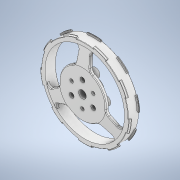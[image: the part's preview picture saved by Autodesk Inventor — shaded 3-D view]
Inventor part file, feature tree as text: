
AUTODESK INVENTOR PART (.ipt)
format: ipt  version: 2021 (Build 250183000, 183)  size: 946,176 bytes
history: native  units: mm
features: sketch x19, extrude x14, fillet x7, pattern_circular x5, revolve x3, other x2, chamfer x2, projected_geometry x2
ambient origin geometry x8: Origin, YZ Plane, XZ Plane, XY Plane, X Axis, Y Axis, Z Axis, Center Point
bodies: Body1 (feature_tree)
feature tree (54):
  other  "ソリッド1"
  extrude  "押し出し1"  Depth=50.6mm
  extrude  "押し出し2"  Depth=7.3mm TaperAngle=0.0deg
  sketch  "スケッチ3"
  revolve  "回転1"
  extrude  "押し出し3"  Depth=3.0mm
  revolve  "回転2"
  chamfer  "面取り1"  Distance=1.3mm
  chamfer  "面取り2"  Distance=26.0mm
  extrude  "押し出し4"  TaperAngle=90.0deg  [1 undecoded]
  pattern_circular  "円形状パターン1"  [2 undecoded]
  extrude  "押し出し5"  Depth=3.0mm
  pattern_circular  "円形状パターン2"  [2 undecoded]
  extrude  "押し出し6"  Depth=4.0mm
  extrude  "押し出し7"  Depth=30.0mm TaperAngle=360.0deg
  revolve  "回転3"
  extrude  "押し出し8"  TaperAngle=0.0deg  [1 undecoded]
  pattern_circular  "円形状パターン3"  [2 undecoded]
  extrude  "押し出し9"  Depth=1.0mm
  extrude  "押し出し10"  Depth=1.0mm
  extrude  "押し出し11"  TaperAngle=90.0deg  [1 undecoded]
  pattern_circular  "円形状パターン4"  Angle=45.0deg  [1 undecoded]
  extrude  "押し出し12"  Depth=0.7mm TaperAngle=45.0deg
  extrude  "押し出し13"  Depth=5.0mm
  pattern_circular  "円形状パターン5"  [2 undecoded]
  sketch  "スケッチ18"
  other  "作業平面1"
  extrude  "押し出し14"  TaperAngle=180.0deg  [1 undecoded]
  fillet  "フィレット1"  Radius=1.3mm
  fillet  "フィレット2"  Radius=90.0mm
  fillet  "フィレット3"  Radius=5.0mm
  fillet  "フィレット4"  Radius=5.0mm
  fillet  "フィレット5"  Radius=1.3mm
  fillet  "フィレット6"  Radius=90.0mm
  fillet  "フィレット7"  Radius=4.5mm
  sketch  "スケッチ1"
  sketch  "スケッチ2"
  sketch  "スケッチ4"
  sketch  "スケッチ5"
  projected_geometry  "投影ループ1"
  projected_geometry  "投影ループ2"
  sketch  "スケッチ6"
  sketch  "スケッチ7"
  sketch  "スケッチ8"
  sketch  "スケッチ9"
  sketch  "スケッチ10"
  sketch  "スケッチ11"
  sketch  "スケッチ12"
  sketch  "スケッチ13"
  sketch  "スケッチ14"
  sketch  "スケッチ15"
  sketch  "スケッチ16"
  sketch  "スケッチ17"
  sketch  "スケッチ19"
note: 13 required parameter values undecoded (feature->parameter linkage not recoverable at this tier; creation-order binding heuristic only, values carry confidence <= 0.55)
